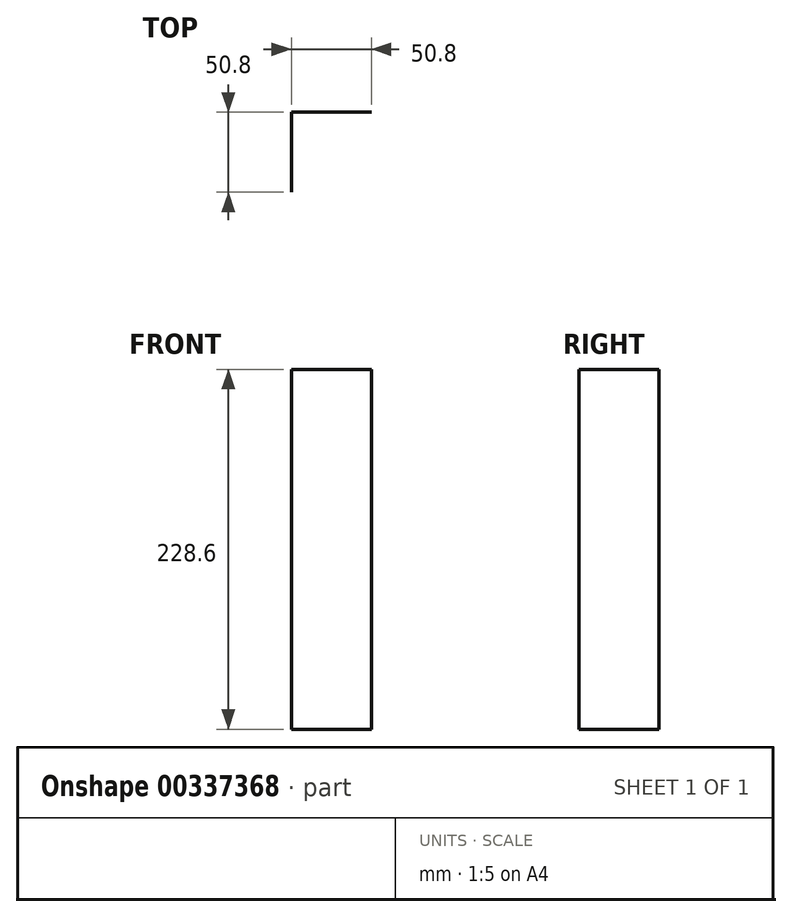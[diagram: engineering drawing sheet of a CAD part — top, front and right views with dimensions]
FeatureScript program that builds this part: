
annotation { "Feature Type Name" : "Feature", "Feature Type Description" : "" }
export const myFeature = defineFeature(function(context is Context, id is Id, definition is map)
    precondition{}
    {
        {
            var Q0;
            Q0=qCreatedBy(makeId("Top.planeOp"),FACE);
            var sketch = newSketch(context, id + "F0", { "sketchPlane" : qUnion([Q0])});
            skLineSegment(sketch, "E0", {"start": v(-61.2, -11.42) * mm, "end": v(-61.2, 39.38) * mm});
            skLineSegment(sketch, "E1", {"start": v(-61.2, 39.38) * mm, "end": v(-10.4, 39.38) * mm});
            skSolve(sketch);
        }
        {
            var Q0;
            Q0 = qSketchRegion(id + "F0", true);
            var Q1;
            Q1=sQuery(id+"F0.wireOp",EDGE,"E1");
            var Q2;
            Q2=sQuery(id+"F0.wireOp",EDGE,"E0");
            extrude(context, id + "F1", {"entities" : qUnion([Q0]), "bodyType" : ToolBodyType.SURFACE, "surfaceEntities" : qUnion([Q1, Q2]), "depth" : 228.6 * mm});
        }
    });
